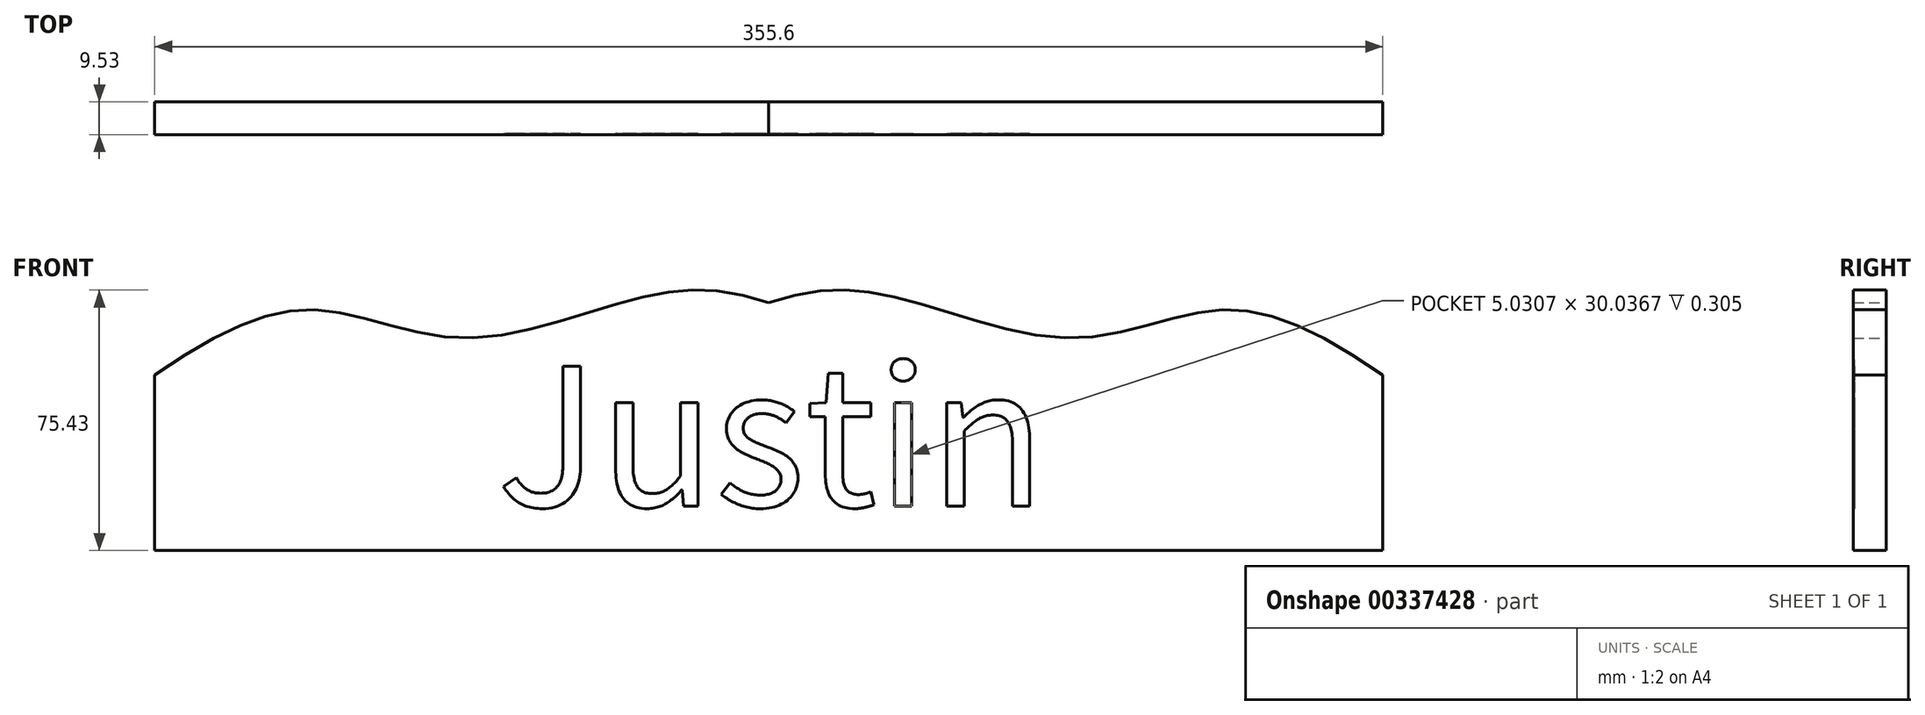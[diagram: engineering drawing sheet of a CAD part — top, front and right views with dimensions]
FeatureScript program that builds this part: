
annotation { "Feature Type Name" : "Feature", "Feature Type Description" : "" }
export const myFeature = defineFeature(function(context is Context, id is Id, definition is map)
    precondition{}
    {
        {
            var Q0;
            Q0=qCreatedBy(makeId("Front.planeOp"),FACE);
            var sketch = newSketch(context, id + "F0", { "sketchPlane" : qUnion([Q0])});
            skLineSegment(sketch, "E0.bottom", {"start": v(-177.8, 0) * mm, "end": v(177.8, 0) * mm});
            skLineSegment(sketch, "E0.left", {"start": v(-177.8, 0) * mm, "end": v(-177.8, 50.8) * mm});
            skLineSegment(sketch, "E0.right", {"start": v(177.8, 0) * mm, "end": v(177.8, 50.8) * mm});
            skFitSpline(sketch, "E1", {"points": [v(-177.8, 50.8) * mm, v(-131.25, 69.68) * mm, v(-88.9, 61.56) * mm, v(-38.3, 72.9) * mm, v(0, 71.73) * mm], "startDerivative": vector(213.33, 145.5) * mm, "endDerivative": vector(183.84, -64.97) * mm});
            skLineSegment(sketch, "E2", {"start": v(0, 76.2) * mm, "end": v(0, 0) * mm, "construction": true});
            skPoint(sketch, "E3.orphan", {"position": v(-177.8, 76.2) * mm});
            skFitSpline(sketch, "E4.MirrorCS", {"points": [v(177.8, 50.8) * mm, v(131.25, 69.68) * mm, v(88.9, 61.56) * mm, v(38.3, 72.9) * mm, v(0, 71.73) * mm], "startDerivative": vector(-213.33, 145.5) * mm, "endDerivative": vector(-183.84, -64.97) * mm});
            skPoint(sketch, "E5.orphan", {"position": v(177.8, 76.2) * mm});
            skSolve(sketch);
        }
        {
            var Q0;
            Q0 = qSketchRegion(id + "F0", true);
            extrude(context, id + "F1", {"entities" : qUnion([Q0]), "depth" : 9.52 * mm});
        }
        {
            var Q0;
            Q0=makeQuery(id+"F1.opExtrude","CAP_FACE",FACE,{"disambiguationData":[OSD([sQuery(id+"F0.wireOp",EDGE,"E0.bottom"),sQuery(id+"F0.wireOp",EDGE,"E0.left"),sQuery(id+"F0.wireOp",EDGE,"E0.right"),sQuery(id+"F0.wireOp",EDGE,"E1"),sQuery(id+"F0.wireOp",EDGE,"E4.MirrorCS")])],"isStart":false});
            var sketch = newSketch(context, id + "F2", { "sketchPlane" : qUnion([Q0])});
            skLineSegment(sketch, "E6", {"start": v(0, 0) * mm, "end": v(0, 66.82) * mm, "construction": true});
            skPoint(sketch, "E6.endSnap0", {"position": v(0, 0) * mm});
            skText(sketch, "E7", { "text": "Justin", "fontName": "NotoSansCJKjp-Regular.otf"});
            const initialGuessF2  = {"E7": [-0.0787, 0.01283, 1, 0, 0.03983]};
            skSetInitialGuess(sketch, initialGuessF2);
            skSolve(sketch);
        }
        {
            var Q0;
            Q0 = qSketchRegion(id + "F2", true);
            extrude(context, id + "F3", {"entities" : qUnion([Q0]), "operationType" : NewBodyOperationType.REMOVE, "oppositeDirection" : true, "depth" : 0.3 * mm});
        }
    });
